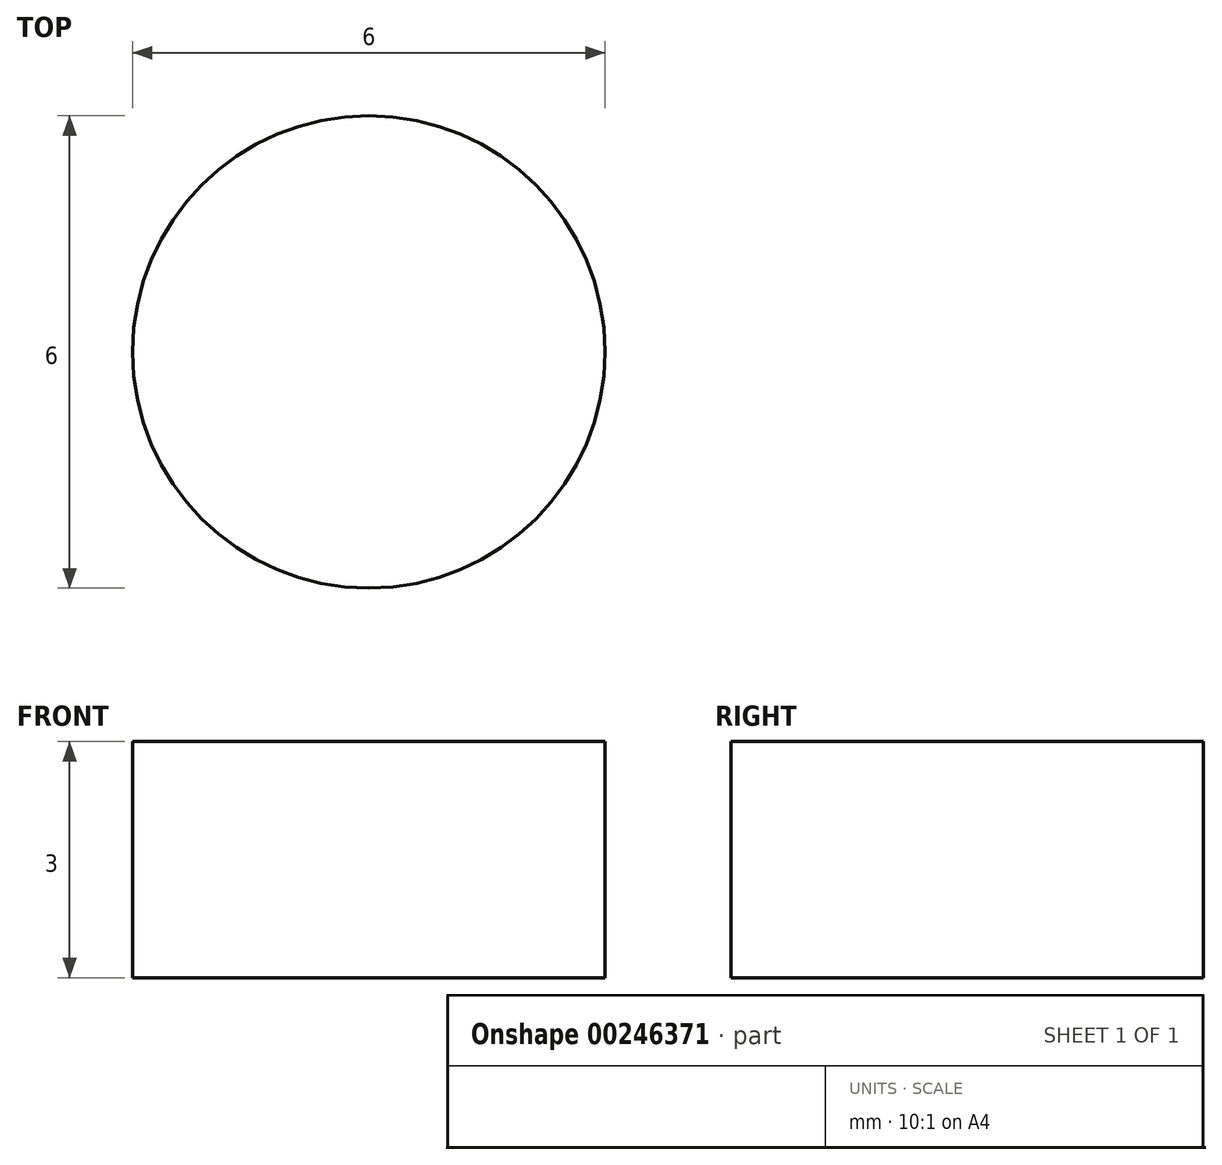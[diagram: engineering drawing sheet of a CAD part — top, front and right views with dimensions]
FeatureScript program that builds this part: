
annotation { "Feature Type Name" : "Feature", "Feature Type Description" : "" }
export const myFeature = defineFeature(function(context is Context, id is Id, definition is map)
    precondition{}
    {
        {
            var Q0;
            Q0=qCreatedBy(makeId("Top.planeOp"),FACE);
            var sketch = newSketch(context, id + "F0", { "sketchPlane" : qUnion([Q0])});
            skCircle(sketch, "E0", {"center": v(0, 0) * mm, "radius": 3 * mm});
            skSolve(sketch);
        }
        {
            var Q0;
            Q0=makeQuery(id+"F0.imprint","IMPRINT",FACE,{"disambiguationData":[TD([[makeQuery(id+"F0.imprint","IMPRINT",EDGE,{"derivedFrom":sQuery(id+"F0.wireOp",EDGE,"E0")}),1.0]])]});
            extrude(context, id + "F1", {"entities" : qUnion([Q0]), "depth" : 3 * mm});
        }
    });
